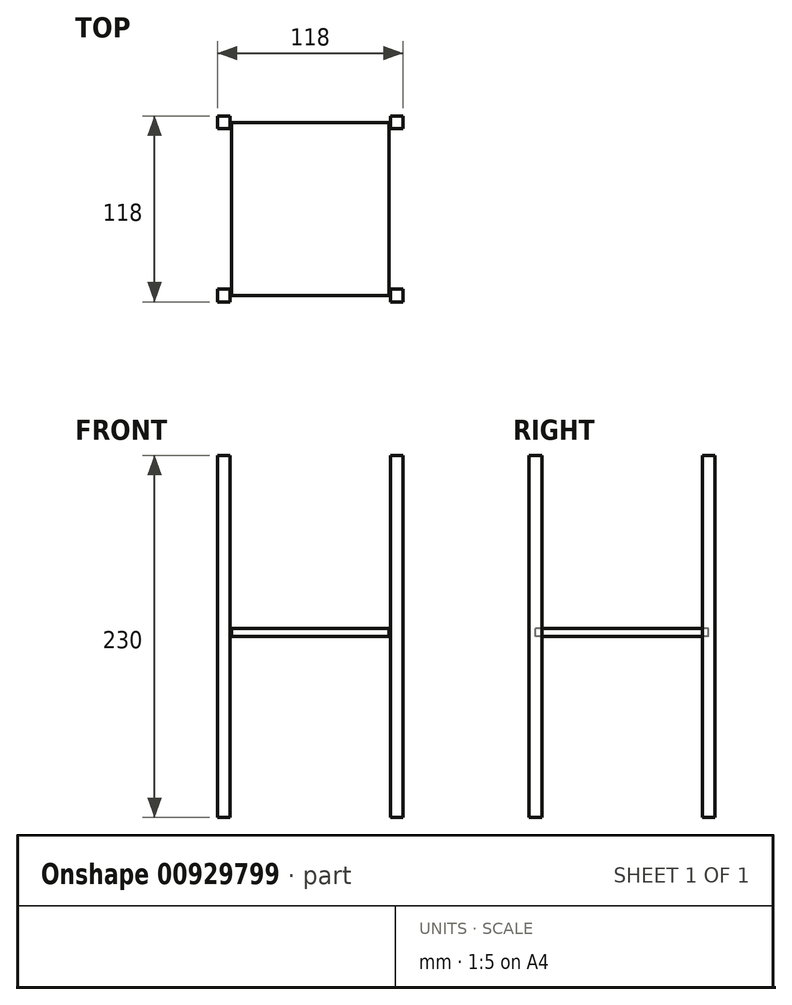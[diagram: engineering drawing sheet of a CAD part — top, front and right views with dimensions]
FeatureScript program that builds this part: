
annotation { "Feature Type Name" : "Feature", "Feature Type Description" : "" }
export const myFeature = defineFeature(function(context is Context, id is Id, definition is map)
    precondition{}
    {
        {
            var Q0;
            Q0=qCreatedBy(makeId("Top.planeOp"),FACE);
            var sketch = newSketch(context, id + "F0", { "sketchPlane" : qUnion([Q0])});
            skLineSegment(sketch, "E0.bottom", {"start": v(55, -55) * mm, "end": v(-55, -55) * mm, "construction": true});
            skLineSegment(sketch, "E0.top", {"start": v(55, 55) * mm, "end": v(-55, 55) * mm, "construction": true});
            skLineSegment(sketch, "E0.left", {"start": v(55, -55) * mm, "end": v(55, 55) * mm, "construction": true});
            skLineSegment(sketch, "E0.right", {"start": v(-55, -55) * mm, "end": v(-55, 55) * mm, "construction": true});
            skPoint(sketch, "E0.middle", {"position": v(0, 0) * mm});
            skLineSegment(sketch, "E1.bottom", {"start": v(-51, 51) * mm, "end": v(-59, 51) * mm});
            skLineSegment(sketch, "E1.top", {"start": v(-51, 59) * mm, "end": v(-59, 59) * mm});
            skLineSegment(sketch, "E1.left", {"start": v(-51, 51) * mm, "end": v(-51, 59) * mm});
            skLineSegment(sketch, "E1.right", {"start": v(-59, 51) * mm, "end": v(-59, 59) * mm});
            skPoint(sketch, "E1.middle", {"position": v(-55, 55) * mm});
            skLineSegment(sketch, "E2.0.1.0", {"start": v(-51, -51) * mm, "end": v(-59, -51) * mm});
            skLineSegment(sketch, "E2.0.1.1", {"start": v(-59, -59) * mm, "end": v(-59, -51) * mm});
            skLineSegment(sketch, "E2.0.1.2", {"start": v(-51, -59) * mm, "end": v(-59, -59) * mm});
            skLineSegment(sketch, "E2.0.1.3", {"start": v(-51, -59) * mm, "end": v(-51, -51) * mm});
            skLineSegment(sketch, "E2.1.0.0", {"start": v(59, 59) * mm, "end": v(51, 59) * mm});
            skLineSegment(sketch, "E2.1.0.1", {"start": v(51, 51) * mm, "end": v(51, 59) * mm});
            skLineSegment(sketch, "E2.1.0.2", {"start": v(59, 51) * mm, "end": v(51, 51) * mm});
            skLineSegment(sketch, "E2.1.0.3", {"start": v(59, 51) * mm, "end": v(59, 59) * mm});
            skLineSegment(sketch, "E2.1.1.0", {"start": v(59, -51) * mm, "end": v(51, -51) * mm});
            skLineSegment(sketch, "E2.1.1.1", {"start": v(51, -59) * mm, "end": v(51, -51) * mm});
            skLineSegment(sketch, "E2.1.1.2", {"start": v(59, -59) * mm, "end": v(51, -59) * mm});
            skLineSegment(sketch, "E2.1.1.3", {"start": v(59, -59) * mm, "end": v(59, -51) * mm});
            skLineSegment(sketch, "E2.direction1", {"start": v(-59, 51) * mm, "end": v(51, 51) * mm, "construction": true});
            skLineSegment(sketch, "E2.direction2", {"start": v(-59, 51) * mm, "end": v(-59, -59) * mm, "construction": true});
            skSolve(sketch);
        }
        {
            var Q0;
            Q0 = qSketchRegion(id + "F0", true);
            extrude(context, id + "F1", {"entities" : qUnion([Q0]), "depth" : 230 * mm, "offsetDistance" : 25 * mm});
        }
        {
            var Q0;
            Q0=qCreatedBy(makeId("Top.planeOp"),FACE);
            cPlane(context, id + "F2", {"entities" : qUnion([Q0]), "cplaneType" : CPlaneType.OFFSET, "offset" : 120 * mm, "width" : 150 * mm, "height" : 150 * mm});
        }
        {
            var Q0;
            Q0=qCreatedBy(id+"F2.planeOp",FACE);
            var sketch = newSketch(context, id + "F3", { "sketchPlane" : qUnion([Q0])});
            skLineSegment(sketch, "E3.bottom", {"start": v(50, 55) * mm, "end": v(-50, 55) * mm});
            skLineSegment(sketch, "E3.top", {"start": v(50, -55) * mm, "end": v(-50, -55) * mm});
            skLineSegment(sketch, "E3.left", {"start": v(50, 55) * mm, "end": v(50, -55) * mm});
            skLineSegment(sketch, "E3.right", {"start": v(-50, 55) * mm, "end": v(-50, -55) * mm});
            skPoint(sketch, "E3.middle", {"position": v(0, 0) * mm});
            skSolve(sketch);
        }
        {
            var Q0;
            Q0=makeQuery(id+"F3.imprint","IMPRINT",FACE,{"disambiguationData":[TD([[makeQuery(id+"F3.imprint","IMPRINT",EDGE,{"derivedFrom":sQuery(id+"F3.wireOp",EDGE,"E3.bottom")}),1.0]])]});
            extrude(context, id + "F4", {"entities" : qUnion([Q0]), "oppositeDirection" : true, "depth" : 5 * mm, "offsetDistance" : 25 * mm});
        }
        {
            var Q0;
            Q0=qCreatedBy(makeId("Front.planeOp"),FACE);
            var sketch = newSketch(context, id + "F5", { "sketchPlane" : qUnion([Q0])});
            skLineSegment(sketch, "E4", {"start": v(-82.23, 206.94) * mm, "end": v(0, 304.94) * mm});
            skLineSegment(sketch, "E5.MirrorCS", {"start": v(82.23, 206.94) * mm, "end": v(0, 304.94) * mm});
            skLineSegment(sketch, "E6", {"start": v(-82.23, 206.94) * mm, "end": v(82.23, 206.94) * mm, "construction": true});
            skSolve(sketch);
        }
        {
            var Q0;
            Q0 = qSketchRegion(id + "F5", true);
            var Q1;
            Q1=sQuery(id+"F5.wireOp",EDGE,"E5.MirrorCS");
            var Q2;
            Q2=sQuery(id+"F5.wireOp",EDGE,"E4");
            extrude(context, id + "F6", {"entities" : qUnion([Q0]), "bodyType" : ToolBodyType.SURFACE, "surfaceEntities" : qUnion([Q1, Q2]), "endBound" : BoundingType.SYMMETRIC, "depth" : 130 * mm, "offsetDistance" : 25 * mm});
        }
    });
